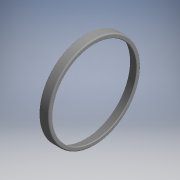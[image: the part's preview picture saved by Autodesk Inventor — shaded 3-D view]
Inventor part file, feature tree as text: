
AUTODESK INVENTOR PART (.ipt)
format: ipt  version: 2017.3 (Build 213256000, 256)  size: 129,024 bytes
history: native  units: mm (DEFAULTED — no unit token found)
features: other x7, revolve x1, sketch x1
ambient origin geometry x8: Origin, YZ Plane, XZ Plane, XY Plane, X Axis, Y Axis, Z Axis, Center Point
bodies: Solid1 (feature_tree)
feature tree (9):
  revolve  "Revolution1"  [1 undecoded]
  other  "outer_ring_XY"
  other  "outer_ring_YZ"
  other  "outer_ring_ZX"
  other  "outer_ring_X"
  other  "outer_ring_Y"
  other  "outer_ring_Z"
  other  "outer_ring_Center"
  sketch  "Sketch_1"  dims[d0=360.0deg]
note: 1 required parameter value undecoded (feature->parameter linkage not recoverable at this tier; creation-order binding heuristic only, values carry confidence <= 0.55)
